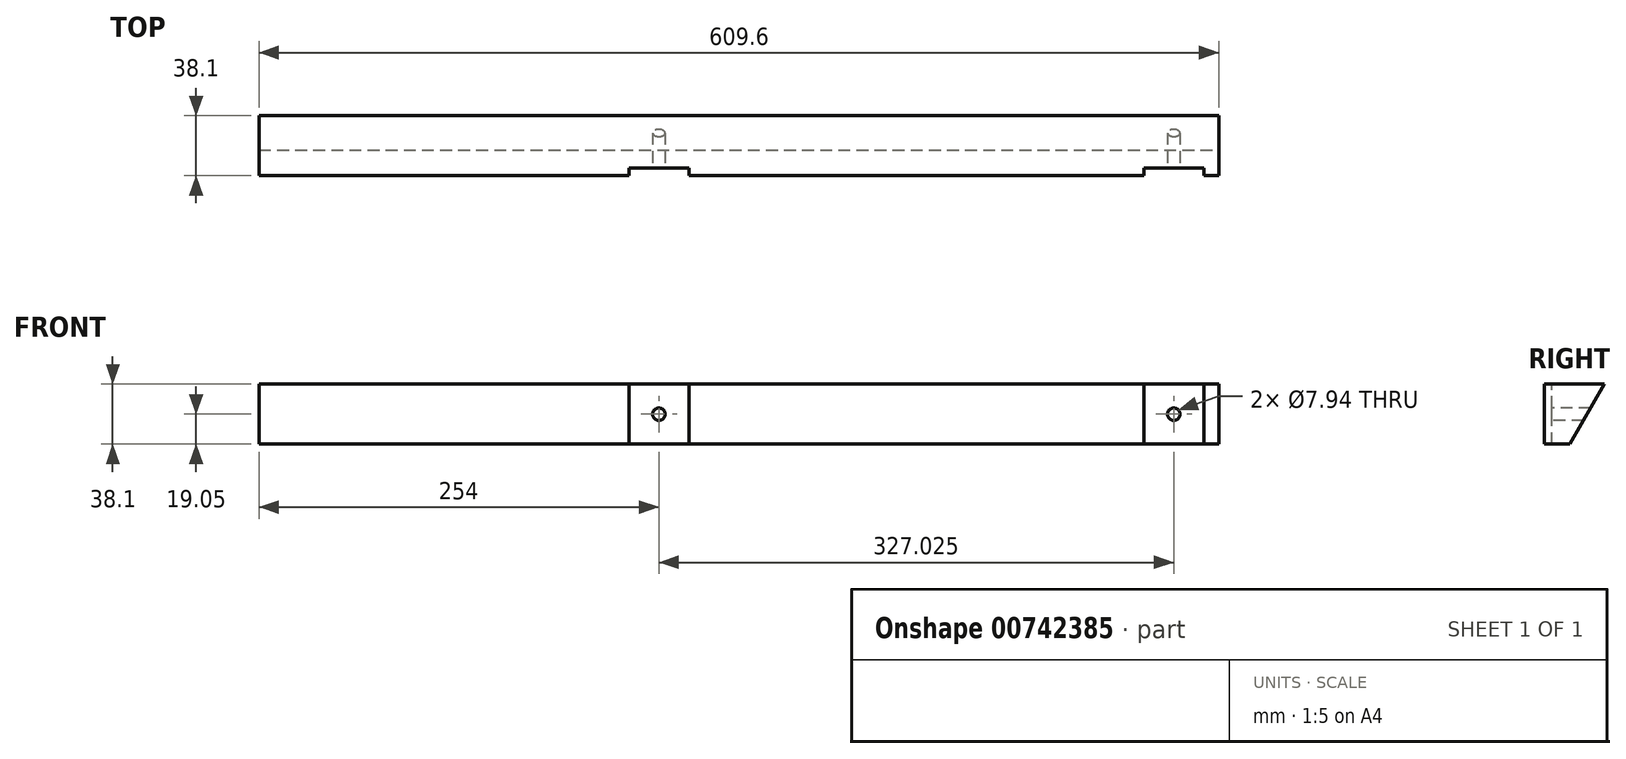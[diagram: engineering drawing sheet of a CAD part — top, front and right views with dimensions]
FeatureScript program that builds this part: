
annotation { "Feature Type Name" : "Feature", "Feature Type Description" : "" }
export const myFeature = defineFeature(function(context is Context, id is Id, definition is map)
    precondition{}
    {
        {
            var Q0;
            Q0=qCreatedBy(makeId("Right.planeOp"),FACE);
            var sketch = newSketch(context, id + "F0", { "sketchPlane" : qUnion([Q0])});
            skLineSegment(sketch, "E0.bottom", {"start": v(0, 0) * mm, "end": v(38.1, 0) * mm});
            skLineSegment(sketch, "E0.top", {"start": v(0, 38.1) * mm, "end": v(38.1, 38.1) * mm});
            skLineSegment(sketch, "E0.left", {"start": v(0, 0) * mm, "end": v(0, 38.1) * mm});
            skLineSegment(sketch, "E0.right", {"start": v(38.1, 0) * mm, "end": v(38.1, 38.1) * mm});
            skSolve(sketch);
        }
        {
            var Q0;
            Q0=makeQuery(id+"F0.imprint","IMPRINT",FACE,{"disambiguationData":[TD([[makeQuery(id+"F0.imprint","IMPRINT",EDGE,{"derivedFrom":sQuery(id+"F0.wireOp",EDGE,"E0.bottom")}),1.0]])]});
            extrude(context, id + "F1", {"entities" : qUnion([Q0]), "depth" : 304.8 * mm, "offsetDistance" : 25.4 * mm, "hasSecondDirection" : true, "secondDirectionOppositeDirection" : true, "secondDirectionDepth" : 304.8 * mm});
        }
        {
            var Q0;
            Q0=makeQuery(id+"F1.opExtrude","SWEPT_FACE",FACE,{"disambiguationData":[OSD([sQuery(id+"F0.wireOp",EDGE,"E0.top")])]});
            var sketch = newSketch(context, id + "F2", { "sketchPlane" : qUnion([Q0])});
            skLineSegment(sketch, "E1", {"start": v(295.28, 0) * mm, "end": v(295.28, 4.76) * mm});
            skLineSegment(sketch, "E2", {"start": v(295.28, 4.76) * mm, "end": v(257.18, 4.76) * mm});
            skLineSegment(sketch, "E3", {"start": v(-69.85, 4.76) * mm, "end": v(-69.85, 0) * mm});
            skLineSegment(sketch, "E4", {"start": v(-69.85, 0) * mm, "end": v(-31.75, 0) * mm});
            skLineSegment(sketch, "E5", {"start": v(257.18, 4.76) * mm, "end": v(257.18, 0) * mm});
            skLineSegment(sketch, "E6", {"start": v(-31.75, 4.76) * mm, "end": v(-31.75, 0) * mm});
            skLineSegment(sketch, "E7.trimOffspring", {"start": v(-31.75, 4.76) * mm, "end": v(-69.85, 4.76) * mm});
            skLineSegment(sketch, "E8.trimOffspring", {"start": v(257.18, 0) * mm, "end": v(295.28, 0) * mm});
            skSolve(sketch);
        }
        {
            var Q0;
            Q0=makeQuery(id+"F2.imprint","IMPRINT",FACE,{"disambiguationData":[TD([[makeQuery(id+"F2.imprint","IMPRINT",EDGE,{"derivedFrom":sQuery(id+"F2.wireOp",EDGE,"E3")}),1.0]])]});
            var Q1;
            Q1=makeQuery(id+"F2.imprint","IMPRINT",FACE,{"disambiguationData":[TD([[makeQuery(id+"F2.imprint","IMPRINT",EDGE,{"derivedFrom":sQuery(id+"F2.wireOp",EDGE,"E1")}),1.0]])]});
            extrude(context, id + "F3", {"entities" : qUnion([Q0, Q1]), "operationType" : NewBodyOperationType.REMOVE, "endBound" : BoundingType.THROUGH_ALL, "oppositeDirection" : true, "depth" : 25.4 * mm, "offsetDistance" : 25.4 * mm});
        }
        {
            var Q0;
            Q0=makeQuery(id+"F3.boolean.opBoolean","COPY",FACE,{"derivedFrom":makeQuery(id+"F3.opExtrude","SWEPT_FACE",FACE,{"disambiguationData":[OSD([sQuery(id+"F2.wireOp",EDGE,"E7.trimOffspring")])]})});
            var sketch = newSketch(context, id + "F4", { "sketchPlane" : qUnion([Q0])});
            skLineSegment(sketch, "E9", {"start": v(-69.85, 19.05) * mm, "end": v(-31.75, 19.05) * mm, "construction": true});
            skLineSegment(sketch, "E10", {"start": v(-50.8, 38.1) * mm, "end": v(-50.8, 0) * mm, "construction": true});
            skPoint(sketch, "E11", {"position": v(-50.8, 19.05) * mm});
            skPoint(sketch, "E12", {"position": v(276.23, 19.05) * mm});
            skSolve(sketch);
        }
        {
            var Q0;
            Q0=sQuery(id+"F4.wireOp",VERTEX,"E11");
            var Q1;
            Q1=sQuery(id+"F4.wireOp",VERTEX,"E12");
            var Q2;
            Q2=makeQuery(id+"F1.opExtrude","SWEPT_BODY",BODY,{"disambiguationData":[OSD([sQuery(id+"F0.wireOp",EDGE,"E0.bottom"),sQuery(id+"F0.wireOp",EDGE,"E0.top"),sQuery(id+"F0.wireOp",EDGE,"E0.left"),sQuery(id+"F0.wireOp",EDGE,"E0.right")])]});
            hole(context, id + "F5", {"style" : HoleStyle.SIMPLE, "endStyle" : HoleEndStyle.THROUGH, "holeDiameter" : 7.94 * mm, "majorDiameter" : 6.35 * mm, "isTappedThrough" : true, "tappedDepth" : 12.7 * mm, "tapClearance" : 3, "locations" : qUnion([Q0, Q1]), "scope" : qUnion([Q2])});
        }
        {
            var Q0;
            Q0=makeQuery(id+"F1.opExtrude","CAP_FACE",FACE,{"disambiguationData":[OSD([sQuery(id+"F0.wireOp",EDGE,"E0.bottom"),sQuery(id+"F0.wireOp",EDGE,"E0.top"),sQuery(id+"F0.wireOp",EDGE,"E0.left"),sQuery(id+"F0.wireOp",EDGE,"E0.right")])],"isStart":false});
            var sketch = newSketch(context, id + "F6", { "sketchPlane" : qUnion([Q0])});
            skLineSegment(sketch, "E13", {"start": v(38.1, 38.1) * mm, "end": v(16.1, 0) * mm});
            skLineSegment(sketch, "E14", {"start": v(16.1, 0) * mm, "end": v(38.1, 0) * mm});
            skLineSegment(sketch, "E15", {"start": v(38.1, 0) * mm, "end": v(38.1, 38.1) * mm});
            skSolve(sketch);
        }
        {
            var Q0;
            Q0=makeQuery(id+"F6.imprint","IMPRINT",FACE,{"disambiguationData":[TD([[makeQuery(id+"F6.imprint","IMPRINT",EDGE,{"derivedFrom":sQuery(id+"F6.wireOp",EDGE,"E13")}),1.0]])]});
            extrude(context, id + "F7", {"entities" : qUnion([Q0]), "operationType" : NewBodyOperationType.REMOVE, "endBound" : BoundingType.THROUGH_ALL, "oppositeDirection" : true, "depth" : 25.4 * mm, "offsetDistance" : 25.4 * mm});
        }
    });
